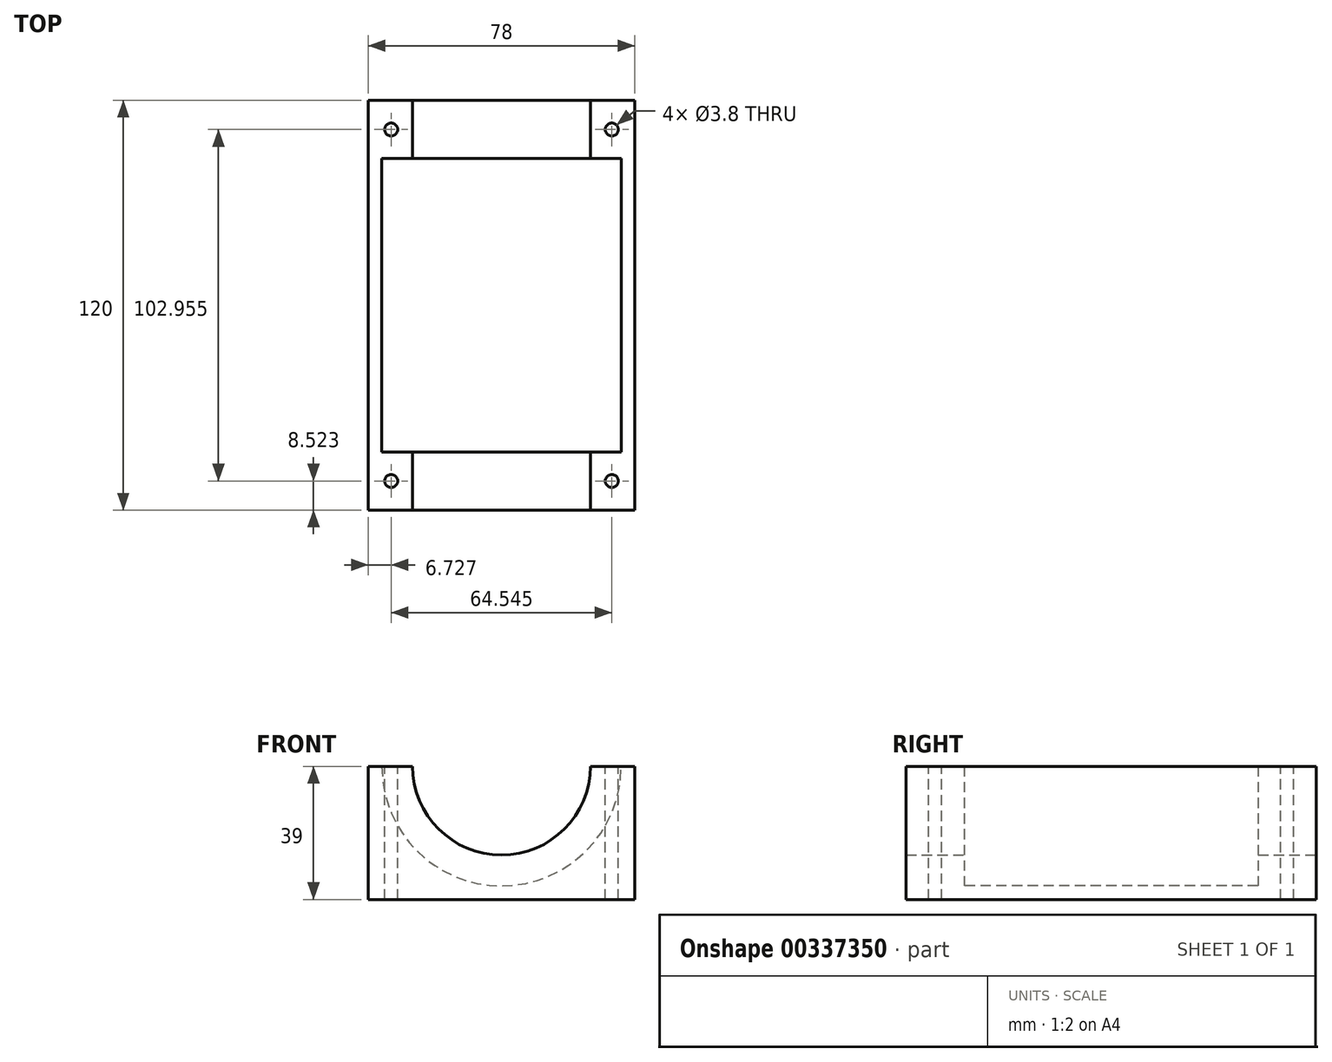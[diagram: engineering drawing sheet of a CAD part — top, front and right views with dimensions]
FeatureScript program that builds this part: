
annotation { "Feature Type Name" : "Feature", "Feature Type Description" : "" }
export const myFeature = defineFeature(function(context is Context, id is Id, definition is map)
    precondition{}
    {
        {
            var Q0;
            Q0=qCreatedBy(makeId("Front.planeOp"),FACE);
            var sketch = newSketch(context, id + "F0", { "sketchPlane" : qUnion([Q0])});
            skLineSegment(sketch, "E0.bottom", {"start": v(39, -19.5) * mm, "end": v(-39, -19.5) * mm});
            skLineSegment(sketch, "E0.left", {"start": v(39, -19.5) * mm, "end": v(39, 19.5) * mm});
            skLineSegment(sketch, "E0.right", {"start": v(-39, -19.5) * mm, "end": v(-39, 19.5) * mm});
            skPoint(sketch, "E0.middle", {"position": v(0, 0) * mm});
            skArc(sketch, "E1", {"start": v(-26, 19.5) * mm, "mid": v(0, -6.5) * mm, "end": v(26, 19.5) * mm});
            skLineSegment(sketch, "E2", {"start": v(-39, 19.5) * mm, "end": v(-26, 19.5) * mm});
            skLineSegment(sketch, "E3", {"start": v(26, 19.5) * mm, "end": v(39, 19.5) * mm});
            skSolve(sketch);
        }
        {
            var Q0;
            Q0=makeQuery(id+"F0.imprint","IMPRINT",FACE,{"disambiguationData":[TD([[makeQuery(id+"F0.imprint","IMPRINT",EDGE,{"derivedFrom":sQuery(id+"F0.wireOp",EDGE,"E0.bottom")}),-1.0]])]});
            extrude(context, id + "F1", {"entities" : qUnion([Q0]), "depth" : 60 * mm, "hasSecondDirection" : true, "secondDirectionOppositeDirection" : true, "secondDirectionDepth" : 60 * mm});
        }
        {
            var Q0;
            Q0=qCreatedBy(makeId("Front.planeOp"),FACE);
            var sketch = newSketch(context, id + "F2", { "sketchPlane" : qUnion([Q0])});
            skCircle(sketch, "E4", {"center": v(0, 19.5) * mm, "radius": 35 * mm});
            skSolve(sketch);
        }
        {
            var Q0;
            Q0 = qSketchRegion(id + "F2", true);
            extrude(context, id + "F3", {"entities" : qUnion([Q0]), "operationType" : NewBodyOperationType.REMOVE, "oppositeDirection" : true, "depth" : 43 * mm, "hasSecondDirection" : true, "secondDirectionOppositeDirection" : false, "secondDirectionDepth" : 43 * mm});
        }
        {
            var Q0;
            Q0=qCreatedBy(makeId("Top.planeOp"),FACE);
            var sketch = newSketch(context, id + "F4", { "sketchPlane" : qUnion([Q0])});
            skCircle(sketch, "E5", {"center": v(-32.27, 51.48) * mm, "radius": 1.9 * mm});
            skCircle(sketch, "E6", {"center": v(32.27, 51.48) * mm, "radius": 1.9 * mm});
            skCircle(sketch, "E7", {"center": v(32.27, -51.48) * mm, "radius": 1.9 * mm});
            skCircle(sketch, "E8", {"center": v(-32.27, -51.48) * mm, "radius": 1.9 * mm});
            skSolve(sketch);
        }
        {
            var Q0;
            Q0 = qSketchRegion(id + "F4", true);
            extrude(context, id + "F5", {"entities" : qUnion([Q0]), "operationType" : NewBodyOperationType.REMOVE, "oppositeDirection" : true, "depth" : 50 * mm, "hasSecondDirection" : true, "secondDirectionOppositeDirection" : false, "secondDirectionDepth" : 50 * mm});
        }
    });
